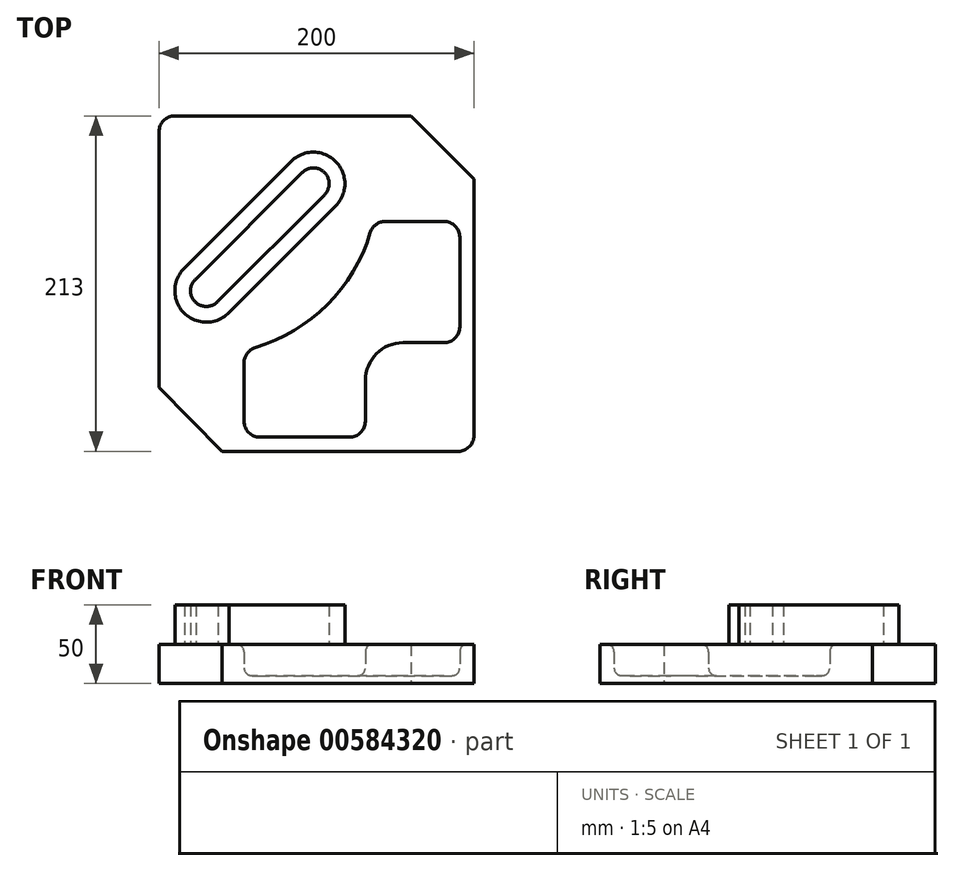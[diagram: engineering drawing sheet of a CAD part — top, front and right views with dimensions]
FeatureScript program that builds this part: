
annotation { "Feature Type Name" : "Feature", "Feature Type Description" : "" }
export const myFeature = defineFeature(function(context is Context, id is Id, definition is map)
    precondition{}
    {
        {
            var Q0;
            Q0=qCreatedBy(makeId("Top.planeOp"),FACE);
            var sketch = newSketch(context, id + "F0", { "sketchPlane" : qUnion([Q0])});
            skPoint(sketch, "E0.MirrorCS.start.orphan", {"position": v(0, 0) * mm});
            skPoint(sketch, "E1.MirrorCS.end.orphan", {"position": v(-100, 106.5) * mm});
            skPoint(sketch, "E2.end.orphan", {"position": v(100, 106.5) * mm});
            skPoint(sketch, "E3.end.orphan", {"position": v(100, -106.5) * mm});
            skLineSegment(sketch, "E4", {"start": v(-100, 106.5) * mm, "end": v(60, 106.5) * mm});
            skLineSegment(sketch, "E5", {"start": v(100, -106.5) * mm, "end": v(100, 66.5) * mm});
            skLineSegment(sketch, "E6.MirrorCS", {"start": v(-100, -65.93) * mm, "end": v(-100, 106.5) * mm});
            skLineSegment(sketch, "E7", {"start": v(-60, -106.5) * mm, "end": v(100, -106.5) * mm});
            skLineSegment(sketch, "E8", {"start": v(-100, -65.93) * mm, "end": v(-60, -106.5) * mm});
            skLineSegment(sketch, "E9", {"start": v(60, 106.5) * mm, "end": v(100, 66.5) * mm});
            skPoint(sketch, "E10.orphan", {"position": v(-100, -106.5) * mm});
            skLineSegment(sketch, "E11", {"start": v(100, -106.5) * mm, "end": v(31, -106.5) * mm, "construction": true});
            skLineSegment(sketch, "E12", {"start": v(31, -97.5) * mm, "end": v(31, -61.5) * mm, "construction": true});
            skLineSegment(sketch, "E13", {"start": v(55, -37.5) * mm, "end": v(81, -37.5) * mm, "construction": true});
            skPoint(sketch, "E14.visualSharp", {"position": v(31, -37.5) * mm});
            skArc(sketch, "E14.filletArc", {"start": v(55, -37.5) * mm, "mid": v(38.03, -44.53) * mm, "end": v(31, -61.5) * mm});
            skLineSegment(sketch, "E15", {"start": v(81, 39.5) * mm, "end": v(36, 39.5) * mm, "construction": true});
            skLineSegment(sketch, "E16", {"start": v(91, -27.5) * mm, "end": v(91, 29.5) * mm, "construction": true});
            skPoint(sketch, "E17.orphan", {"position": v(100, 39.5) * mm});
            skPoint(sketch, "E18.end.orphan", {"position": v(100, -37.5) * mm});
            skPoint(sketch, "E19.visualSharp", {"position": v(91, -37.5) * mm});
            skArc(sketch, "E19.filletArc", {"start": v(81, -37.5) * mm, "mid": v(88.07, -34.57) * mm, "end": v(91, -27.5) * mm});
            skPoint(sketch, "E20.visualSharp", {"position": v(91, 39.5) * mm});
            skArc(sketch, "E20.filletArc", {"start": v(91, 29.5) * mm, "mid": v(88.07, 36.57) * mm, "end": v(81, 39.5) * mm});
            skLineSegment(sketch, "E21", {"start": v(100, -106.5) * mm, "end": v(-46, -106.5) * mm, "construction": true});
            skLineSegment(sketch, "E22", {"start": v(31, -97.5) * mm, "end": v(-46, -97.5) * mm, "construction": true});
            skLineSegment(sketch, "E23", {"start": v(-46, -42.5) * mm, "end": v(-46, -97.5) * mm, "construction": true});
            skLineSegment(sketch, "E24", {"start": v(100, -106.5) * mm, "end": v(-70, -106.5) * mm, "construction": true});
            skLineSegment(sketch, "E25", {"start": v(-70, -106.5) * mm, "end": v(-70, 63.5) * mm, "construction": true});
            skLineSegment(sketch, "E26", {"start": v(-70, 63.5) * mm, "end": v(100, 63.5) * mm, "construction": true});
            skArc(sketch, "E27", {"start": v(-38.86, -40.63) * mm, "mid": v(6.85, -13.35) * mm, "end": v(34.13, 32.36) * mm});
            skLineSegment(sketch, "E28", {"start": v(-46, -50.2) * mm, "end": v(-46, -87.5) * mm});
            skLineSegment(sketch, "E29", {"start": v(31, -87.5) * mm, "end": v(31, -61.5) * mm});
            skLineSegment(sketch, "E30", {"start": v(21, -97.5) * mm, "end": v(-36, -97.5) * mm});
            skLineSegment(sketch, "E31", {"start": v(43.7, 39.5) * mm, "end": v(81, 39.5) * mm});
            skLineSegment(sketch, "E32", {"start": v(91, 29.5) * mm, "end": v(91, -27.5) * mm});
            skLineSegment(sketch, "E33", {"start": v(81, -37.5) * mm, "end": v(55, -37.5) * mm});
            skPoint(sketch, "E34.visualSharp", {"position": v(36, 39.5) * mm});
            skArc(sketch, "E34.filletArc", {"start": v(43.7, 39.5) * mm, "mid": v(37.74, 37.52) * mm, "end": v(34.13, 32.36) * mm});
            skPoint(sketch, "E35.visualSharp", {"position": v(-46, -42.5) * mm});
            skArc(sketch, "E35.filletArc", {"start": v(-38.86, -40.63) * mm, "mid": v(-44.02, -44.24) * mm, "end": v(-46, -50.2) * mm});
            skPoint(sketch, "E36.visualSharp", {"position": v(-46, -97.5) * mm});
            skArc(sketch, "E36.filletArc", {"start": v(-46, -87.5) * mm, "mid": v(-43.07, -94.57) * mm, "end": v(-36, -97.5) * mm});
            skPoint(sketch, "E37.visualSharp", {"position": v(31, -97.5) * mm});
            skArc(sketch, "E37.filletArc", {"start": v(21, -97.5) * mm, "mid": v(28.07, -94.57) * mm, "end": v(31, -87.5) * mm});
            skSolve(sketch);
        }
        {
            var Q0;
            Q0=makeQuery(id+"F0.imprint","IMPRINT",FACE,{"disambiguationData":[TD([[makeQuery(id+"F0.imprint","IMPRINT",EDGE,{"derivedFrom":sQuery(id+"F0.wireOp",EDGE,"E4")}),-1.0]])]});
            extrude(context, id + "F1", {"entities" : qUnion([Q0]), "depth" : 25 * mm, "offsetDistance" : 25 * mm});
        }
        {
            var Q0;
            Q0=makeQuery(id+"F1.opExtrude","CAP_FACE",FACE,{"disambiguationData":[OSD([sQuery(id+"F0.wireOp",EDGE,"E4"),sQuery(id+"F0.wireOp",EDGE,"E5"),sQuery(id+"F0.wireOp",EDGE,"E6.MirrorCS"),sQuery(id+"F0.wireOp",EDGE,"E7"),sQuery(id+"F0.wireOp",EDGE,"E8"),sQuery(id+"F0.wireOp",EDGE,"E9"),sQuery(id+"F0.wireOp",EDGE,"E14.filletArc"),sQuery(id+"F0.wireOp",EDGE,"E19.filletArc"),sQuery(id+"F0.wireOp",EDGE,"E20.filletArc"),sQuery(id+"F0.wireOp",EDGE,"E27"),sQuery(id+"F0.wireOp",EDGE,"E28"),sQuery(id+"F0.wireOp",EDGE,"E29"),sQuery(id+"F0.wireOp",EDGE,"E30"),sQuery(id+"F0.wireOp",EDGE,"E31"),sQuery(id+"F0.wireOp",EDGE,"E32"),sQuery(id+"F0.wireOp",EDGE,"E33"),sQuery(id+"F0.wireOp",EDGE,"E34.filletArc"),sQuery(id+"F0.wireOp",EDGE,"E35.filletArc"),sQuery(id+"F0.wireOp",EDGE,"E36.filletArc"),sQuery(id+"F0.wireOp",EDGE,"E37.filletArc")])],"isStart":true});
            cPlane(context, id + "F2", {"entities" : qUnion([Q0]), "cplaneType" : CPlaneType.OFFSET, "offset" : 25 * mm, "oppositeDirection" : true, "width" : 150 * mm, "height" : 150 * mm});
        }
        {
            var Q0;
            Q0=qCreatedBy(id+"F2.planeOp",FACE);
            var sketch = newSketch(context, id + "F3", { "sketchPlane" : qUnion([Q0])});
            skLineSegment(sketch, "E38.0.0", {"start": v(-100, 65.93) * mm, "end": v(-60, 106.5) * mm});
            skLineSegment(sketch, "E38.0.1", {"start": v(-60, 106.5) * mm, "end": v(100, 106.5) * mm});
            skLineSegment(sketch, "E38.0.2", {"start": v(100, 106.5) * mm, "end": v(100, -66.5) * mm});
            skLineSegment(sketch, "E38.0.3", {"start": v(100, -66.5) * mm, "end": v(60, -106.5) * mm});
            skLineSegment(sketch, "E38.0.4", {"start": v(60, -106.5) * mm, "end": v(-100, -106.5) * mm});
            skLineSegment(sketch, "E38.0.5", {"start": v(-100, -106.5) * mm, "end": v(-100, 65.93) * mm});
            skLineSegment(sketch, "E39.0", {"start": v(43.7, -39.5) * mm, "end": v(81, -39.5) * mm});
            skPoint(sketch, "E40.0", {"position": v(37.74, -37.52) * mm});
            skPoint(sketch, "E41.0", {"position": v(34.13, -32.36) * mm});
            skArc(sketch, "E42.0", {"start": v(-38.86, 40.63) * mm, "mid": v(6.85, 13.35) * mm, "end": v(34.13, -32.36) * mm});
            skLineSegment(sketch, "E43.0", {"start": v(-46, 50.2) * mm, "end": v(-46, 87.5) * mm});
            skPoint(sketch, "E44.0", {"position": v(-46, 68.85) * mm});
            skLineSegment(sketch, "E45.0", {"start": v(21, 97.5) * mm, "end": v(-36, 97.5) * mm});
            skArc(sketch, "E46.0", {"start": v(-46, 87.5) * mm, "mid": v(-43.07, 94.57) * mm, "end": v(-36, 97.5) * mm});
            skPoint(sketch, "E47.0", {"position": v(-36, 97.5) * mm});
            skArc(sketch, "E48.0", {"start": v(21, 97.5) * mm, "mid": v(28.07, 94.57) * mm, "end": v(31, 87.5) * mm});
            skLineSegment(sketch, "E49.0", {"start": v(31, 87.5) * mm, "end": v(31, 61.5) * mm});
            skPoint(sketch, "E50.0", {"position": v(31, 74.5) * mm});
            skArc(sketch, "E51.0", {"start": v(55, 37.5) * mm, "mid": v(38.03, 44.53) * mm, "end": v(31, 61.5) * mm});
            skLineSegment(sketch, "E52.0", {"start": v(81, 37.5) * mm, "end": v(55, 37.5) * mm});
            skPoint(sketch, "E53.0", {"position": v(81, 37.5) * mm});
            skArc(sketch, "E54.0", {"start": v(81, 37.5) * mm, "mid": v(88.07, 34.57) * mm, "end": v(91, 27.5) * mm});
            skLineSegment(sketch, "E55.0", {"start": v(91, -29.5) * mm, "end": v(91, 27.5) * mm});
            skArc(sketch, "E56.0", {"start": v(91, -29.5) * mm, "mid": v(88.07, -36.57) * mm, "end": v(81, -39.5) * mm});
            skPoint(sketch, "E57.0", {"position": v(88.07, -36.57) * mm});
            skPoint(sketch, "E58.0", {"position": v(-44.02, 44.24) * mm});
            skArc(sketch, "E59.0", {"start": v(-38.86, 40.63) * mm, "mid": v(-44.02, 44.24) * mm, "end": v(-46, 50.2) * mm});
            skArc(sketch, "E60", {"start": v(34.13, -32.36) * mm, "mid": v(6.85, 13.35) * mm, "end": v(-38.86, 40.63) * mm});
            skLineSegment(sketch, "E61", {"start": v(31, 61.5) * mm, "end": v(31, 87.5) * mm});
            skLineSegment(sketch, "E62", {"start": v(-46, 87.5) * mm, "end": v(-46, 50.2) * mm});
            skArc(sketch, "E63", {"start": v(-46, 50.2) * mm, "mid": v(-44.02, 44.24) * mm, "end": v(-38.86, 40.63) * mm});
            skArc(sketch, "E64", {"start": v(-36, 97.5) * mm, "mid": v(-43.07, 94.57) * mm, "end": v(-46, 87.5) * mm});
            skArc(sketch, "E65", {"start": v(31, 87.5) * mm, "mid": v(28.07, 94.57) * mm, "end": v(21, 97.5) * mm});
            skArc(sketch, "E66", {"start": v(31, 61.5) * mm, "mid": v(38.03, 44.53) * mm, "end": v(55, 37.5) * mm});
            skArc(sketch, "E67.0", {"start": v(43.7, -39.5) * mm, "mid": v(37.74, -37.52) * mm, "end": v(34.13, -32.36) * mm});
            skArc(sketch, "E68", {"start": v(34.13, -32.36) * mm, "mid": v(37.74, -37.52) * mm, "end": v(43.7, -39.5) * mm});
            skArc(sketch, "E69", {"start": v(81, -39.5) * mm, "mid": v(88.07, -36.57) * mm, "end": v(91, -29.5) * mm});
            skArc(sketch, "E70", {"start": v(91, 27.5) * mm, "mid": v(88.07, 34.57) * mm, "end": v(81, 37.5) * mm});
            skLineSegment(sketch, "E71", {"start": v(100, 106.5) * mm, "end": v(-70, 106.5) * mm, "construction": true});
            skLineSegment(sketch, "E72", {"start": v(-70, 106.5) * mm, "end": v(-70, 4.5) * mm, "construction": true});
            skLineSegment(sketch, "E73", {"start": v(100, 106.5) * mm, "end": v(100, -63.5) * mm, "construction": true});
            skLineSegment(sketch, "E74", {"start": v(100, -63.5) * mm, "end": v(-2, -63.5) * mm, "construction": true});
            skArc(sketch, "E75", {"start": v(-62.52, 11.14) * mm, "mid": v(-77.07, 11.57) * mm, "end": v(-76.64, -2.97) * mm});
            skArc(sketch, "E76", {"start": v(-55.45, 18.22) * mm, "mid": v(-84.14, 18.64) * mm, "end": v(-83.72, -10.05) * mm});
            skArc(sketch, "E77", {"start": v(-9.07, -70.57) * mm, "mid": v(5.07, -70.57) * mm, "end": v(5.07, -56.43) * mm});
            skArc(sketch, "E78", {"start": v(-16.14, -77.64) * mm, "mid": v(12.14, -77.64) * mm, "end": v(12.14, -49.36) * mm});
            skLineSegment(sketch, "E79", {"start": v(-83.72, -10.05) * mm, "end": v(-16.14, -77.64) * mm});
            skLineSegment(sketch, "E80", {"start": v(-83.72, -10.05) * mm, "end": v(-55.45, 18.22) * mm, "construction": true});
            skLineSegment(sketch, "E81", {"start": v(-55.45, 18.22) * mm, "end": v(12.14, -49.36) * mm});
            skLineSegment(sketch, "E82", {"start": v(-76.64, -2.97) * mm, "end": v(-9.07, -70.57) * mm});
            skLineSegment(sketch, "E83", {"start": v(-62.52, 11.14) * mm, "end": v(5.07, -56.43) * mm});
            skLineSegment(sketch, "E84", {"start": v(-16.14, -77.64) * mm, "end": v(12.14, -49.36) * mm, "construction": true});
            skSolve(sketch);
        }
        {
            var Q0;
            Q0=makeQuery(id+"F3.imprint","IMPRINT",FACE,{"disambiguationData":[TD([[makeQuery(id+"F3.imprint","IMPRINT",EDGE,{"derivedFrom":sQuery(id+"F3.wireOp",EDGE,"E75")}),-1.0]])]});
            extrude(context, id + "F4", {"entities" : qUnion([Q0]), "operationType" : NewBodyOperationType.ADD, "oppositeDirection" : true, "depth" : 25 * mm, "offsetDistance" : 25 * mm});
        }
        {
            var Q0;
            Q0=makeQuery(id+"F0.imprint","IMPRINT",FACE,{"disambiguationData":[TD([[makeQuery(id+"F0.imprint","IMPRINT",EDGE,{"derivedFrom":sQuery(id+"F0.wireOp",EDGE,"E14.filletArc")}),-1.0]])]});
            extrude(context, id + "F5", {"entities" : qUnion([Q0]), "operationType" : NewBodyOperationType.ADD, "depth" : 5 * mm, "offsetDistance" : 25 * mm});
        }
        {
            var Q0;
            Q0=makeQuery(id+"F4.opExtrude","CAP_EDGE",EDGE,{"disambiguationData":[OSD([sQuery(id+"F3.wireOp",EDGE,"E76")])],"isStart":true});
            var Q1;
            Q1=makeQuery(id+"F4.opExtrude","CAP_EDGE",EDGE,{"disambiguationData":[OSD([sQuery(id+"F3.wireOp",EDGE,"E81")])],"isStart":true});
            var Q2;
            Q2=makeQuery(id+"F1.opExtrude","CAP_EDGE",EDGE,{"disambiguationData":[OSD([sQuery(id+"F0.wireOp",EDGE,"E27")])],"isStart":false});
            var Q3;
            Q3=makeQuery(id+"F5.opExtrude","CAP_FACE",FACE,{"disambiguationData":[OSD([sQuery(id+"F0.wireOp",EDGE,"E14.filletArc"),sQuery(id+"F0.wireOp",EDGE,"E19.filletArc"),sQuery(id+"F0.wireOp",EDGE,"E20.filletArc"),sQuery(id+"F0.wireOp",EDGE,"E27"),sQuery(id+"F0.wireOp",EDGE,"E28"),sQuery(id+"F0.wireOp",EDGE,"E29"),sQuery(id+"F0.wireOp",EDGE,"E30"),sQuery(id+"F0.wireOp",EDGE,"E31"),sQuery(id+"F0.wireOp",EDGE,"E32"),sQuery(id+"F0.wireOp",EDGE,"E33"),sQuery(id+"F0.wireOp",EDGE,"E34.filletArc"),sQuery(id+"F0.wireOp",EDGE,"E35.filletArc"),sQuery(id+"F0.wireOp",EDGE,"E36.filletArc"),sQuery(id+"F0.wireOp",EDGE,"E37.filletArc")])],"isStart":false});
            fillet(context, id + "F6", {"entities" : qUnion([Q0, Q1, Q2, Q3]), "radius" : 5 * mm, "tangentPropagation" : true, "allowEdgeOverflow" : false});
        }
        {
            var Q0;
            Q0=makeQuery(id+"F1.opExtrude","SWEPT_EDGE",EDGE,{"disambiguationData":[OSD([sQuery(id+"F0.wireOp",EDGE,"E4"),sQuery(id+"F0.wireOp",EDGE,"E6.MirrorCS")])]});
            var Q1;
            Q1=makeQuery(id+"F1.opExtrude","SWEPT_EDGE",EDGE,{"disambiguationData":[OSD([sQuery(id+"F0.wireOp",EDGE,"E5"),sQuery(id+"F0.wireOp",EDGE,"E7")])]});
            fillet(context, id + "F7", {"entities" : qUnion([Q0, Q1]), "radius" : 10 * mm, "tangentPropagation" : true, "allowEdgeOverflow" : false});
        }
    });
